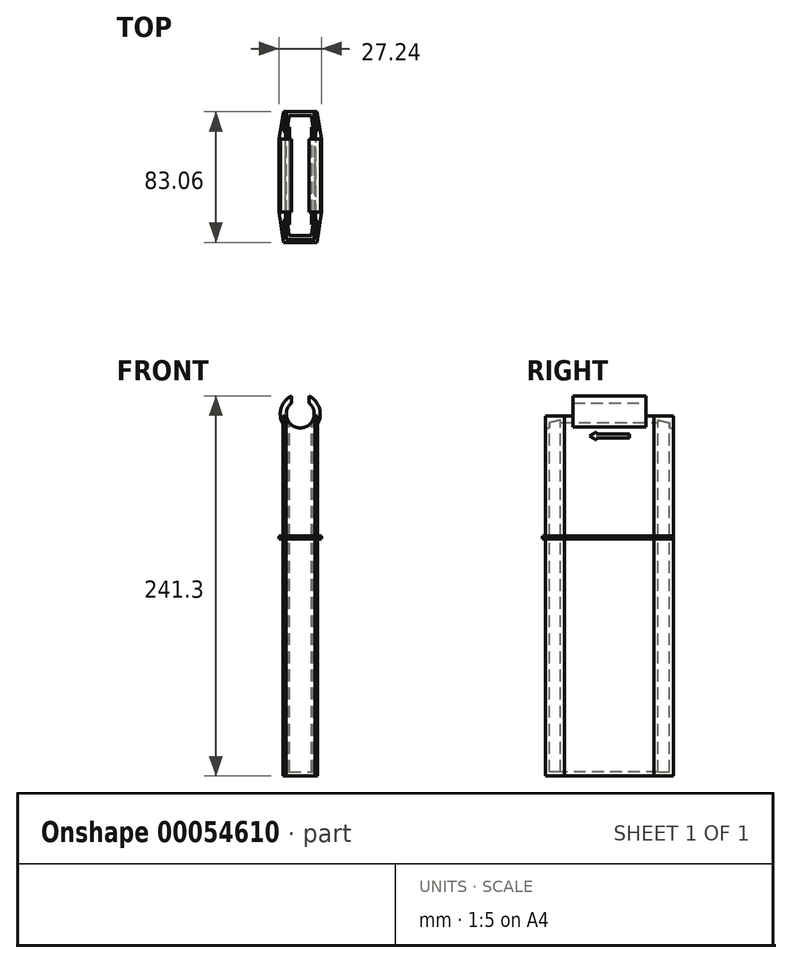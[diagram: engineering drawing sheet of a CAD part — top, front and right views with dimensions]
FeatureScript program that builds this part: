
annotation { "Feature Type Name" : "Feature", "Feature Type Description" : "" }
export const myFeature = defineFeature(function(context is Context, id is Id, definition is map)
    precondition{}
    {
        {
            var Q0;
            Q0=qCreatedBy(makeId("Top.planeOp"),FACE);
            cPlane(context, id + "F0", {"entities" : qUnion([Q0]), "cplaneType" : CPlaneType.OFFSET, "offset" : 76.2 * mm, "oppositeDirection" : true, "width" : 152.4 * mm, "height" : 152.4 * mm});
        }
        {
            var Q0;
            Q0=qCreatedBy(makeId("Top.planeOp"),FACE);
            var sketch = newSketch(context, id + "F1", { "sketchPlane" : qUnion([Q0])});
            skLineSegment(sketch, "E0", {"start": v(0, 97.88) * mm, "end": v(0, -104.86) * mm, "construction": true});
            skPoint(sketch, "E1.rect.middle", {"position": v(0, 0) * mm});
            skLineSegment(sketch, "E2", {"start": v(-10.99, 28.38) * mm, "end": v(-9.2, 40.64) * mm});
            skLineSegment(sketch, "E3", {"start": v(-9.2, 40.64) * mm, "end": v(9.2, 40.64) * mm});
            skLineSegment(sketch, "E4", {"start": v(9.2, 40.64) * mm, "end": v(10.99, 28.38) * mm});
            skLineSegment(sketch, "E5", {"start": v(-10.99, 28.38) * mm, "end": v(-9.52, 28.38) * mm});
            skLineSegment(sketch, "E6", {"start": v(-9.52, 28.38) * mm, "end": v(-9.52, -28.38) * mm});
            skLineSegment(sketch, "E7", {"start": v(-9.52, -28.38) * mm, "end": v(-10.99, -28.38) * mm});
            skLineSegment(sketch, "E8", {"start": v(-10.99, -28.38) * mm, "end": v(-9.2, -40.64) * mm});
            skLineSegment(sketch, "E9", {"start": v(-9.2, -40.64) * mm, "end": v(9.2, -40.64) * mm});
            skLineSegment(sketch, "E10", {"start": v(9.2, -40.64) * mm, "end": v(10.99, -28.38) * mm});
            skLineSegment(sketch, "E11", {"start": v(10.99, -28.38) * mm, "end": v(9.53, -28.38) * mm});
            skLineSegment(sketch, "E12", {"start": v(9.53, -28.38) * mm, "end": v(9.53, 28.38) * mm});
            skLineSegment(sketch, "E13", {"start": v(9.53, 28.38) * mm, "end": v(10.99, 28.38) * mm});
            skLineSegment(sketch, "E14", {"start": v(-33.77, 40.64) * mm, "end": v(28.62, 40.64) * mm, "construction": true});
            skLineSegment(sketch, "E15", {"start": v(-32.51, -40.64) * mm, "end": v(39.56, -40.64) * mm, "construction": true});
            skLineSegment(sketch, "E16", {"start": v(42.78, 0) * mm, "end": v(-43.09, 0) * mm, "construction": true});
            skSolve(sketch);
        }
        {
            var Q0;
            Q0=makeQuery(id+"F1.imprint","IMPRINT",FACE,{"disambiguationData":[TD([[makeQuery(id+"F1.imprint","IMPRINT",EDGE,{"derivedFrom":sQuery(id+"F1.wireOp",EDGE,"E2")}),-1.0]])]});
            extrude(context, id + "F2", {"entities" : qUnion([Q0]), "oppositeDirection" : true, "depth" : 228.6 * mm});
        }
        {
            var Q0;
            Q0=makeQuery(id+"F2.opExtrude","CAP_FACE",FACE,{"disambiguationData":[OSD([sQuery(id+"F1.wireOp",EDGE,"E2"),sQuery(id+"F1.wireOp",EDGE,"E3"),sQuery(id+"F1.wireOp",EDGE,"E4"),sQuery(id+"F1.wireOp",EDGE,"E5"),sQuery(id+"F1.wireOp",EDGE,"E6"),sQuery(id+"F1.wireOp",EDGE,"E7"),sQuery(id+"F1.wireOp",EDGE,"E8"),sQuery(id+"F1.wireOp",EDGE,"E9"),sQuery(id+"F1.wireOp",EDGE,"E10"),sQuery(id+"F1.wireOp",EDGE,"E11"),sQuery(id+"F1.wireOp",EDGE,"E12"),sQuery(id+"F1.wireOp",EDGE,"E13")])],"isStart":true});
            shell(context, id + "F3", {"entities" : qUnion([Q0]), "thickness" : 2.54 * mm});
        }
        {
            var Q0;
            Q0=qCreatedBy(makeId("Front.planeOp"),FACE);
            var sketch = newSketch(context, id + "F4", { "sketchPlane" : qUnion([Q0])});
            skLineSegment(sketch, "E17", {"start": v(0, 1.27) * mm, "end": v(0, 0) * mm, "construction": true});
            skArc(sketch, "E18", {"start": v(-5.54, 12.7) * mm, "mid": v(-12.67, 2.1) * mm, "end": v(-6.99, -9.34) * mm});
            skLineSegment(sketch, "E19", {"start": v(0, 1.27) * mm, "end": v(0, 13.97) * mm, "construction": true});
            skLineSegment(sketch, "E20", {"start": v(5.54, 12.7) * mm, "end": v(-5.54, 12.7) * mm, "construction": true});
            skArc(sketch, "E21", {"start": v(-5.54, 8.22) * mm, "mid": v(-8.83, 2.3) * mm, "end": v(-6.99, -4.23) * mm});
            skLineSegment(sketch, "E22", {"start": v(-5.54, 12.7) * mm, "end": v(-5.54, 8.22) * mm});
            skLineSegment(sketch, "E23", {"start": v(5.54, 12.7) * mm, "end": v(5.54, 8.22) * mm});
            skLineSegment(sketch, "E24", {"start": v(-6.98, -4.23) * mm, "end": v(-6.98, -9.34) * mm});
            skLineSegment(sketch, "E25", {"start": v(6.99, -4.23) * mm, "end": v(6.99, -9.34) * mm});
            skArc(sketch, "E26.trimOffspring", {"start": v(6.98, -4.23) * mm, "mid": v(8.83, 2.3) * mm, "end": v(5.54, 8.22) * mm});
            skArc(sketch, "E27.trimOffspring", {"start": v(6.98, -9.34) * mm, "mid": v(12.67, 2.1) * mm, "end": v(5.54, 12.7) * mm});
            skSolve(sketch);
        }
        {
            var Q0;
            Q0=makeQuery(id+"F4.imprint","IMPRINT",FACE,{"disambiguationData":[TD([[makeQuery(id+"F4.imprint","IMPRINT",EDGE,{"derivedFrom":sQuery(id+"F4.wireOp",EDGE,"E18")}),1.0]])]});
            var Q1;
            Q1=makeQuery(id+"F4.imprint","IMPRINT",FACE,{"disambiguationData":[TD([[makeQuery(id+"F4.imprint","IMPRINT",EDGE,{"derivedFrom":sQuery(id+"F4.wireOp",EDGE,"E23")}),1.0]])]});
            extrude(context, id + "F5", {"entities" : qUnion([Q0, Q1]), "operationType" : NewBodyOperationType.ADD, "endBound" : BoundingType.SYMMETRIC, "depth" : 46.23 * mm});
        }
        {
            var Q0;
            Q0=qCreatedBy(id+"F0.planeOp",FACE);
            var sketch = newSketch(context, id + "F6", { "sketchPlane" : qUnion([Q0])});
            skLineSegment(sketch, "E28", {"start": v(-13.62, -23.11) * mm, "end": v(-10.8, -42.42) * mm});
            skLineSegment(sketch, "E29", {"start": v(-10.8, -42.42) * mm, "end": v(10.8, -42.42) * mm});
            skLineSegment(sketch, "E30", {"start": v(10.8, -42.42) * mm, "end": v(13.62, -23.11) * mm});
            skLineSegment(sketch, "E31", {"start": v(13.62, -23.11) * mm, "end": v(13.62, 23.11) * mm});
            skLineSegment(sketch, "E32", {"start": v(13.62, 23.11) * mm, "end": v(10.52, 40.64) * mm});
            skLineSegment(sketch, "E33", {"start": v(10.52, 40.64) * mm, "end": v(-10.52, 40.64) * mm});
            skLineSegment(sketch, "E34", {"start": v(-10.52, 40.64) * mm, "end": v(-13.62, 23.11) * mm});
            skLineSegment(sketch, "E35", {"start": v(-13.62, 23.11) * mm, "end": v(-13.62, -23.11) * mm});
            skLineSegment(sketch, "E36", {"start": v(23.2, -23.11) * mm, "end": v(-20.93, -23.11) * mm, "construction": true});
            skLineSegment(sketch, "E37", {"start": v(19.25, 23.11) * mm, "end": v(-22.8, 23.11) * mm, "construction": true});
            skLineSegment(sketch, "E38", {"start": v(0, -56.67) * mm, "end": v(0, 46.95) * mm, "construction": true});
            skLineSegment(sketch, "E39", {"start": v(6.66, -70.61) * mm, "end": v(4.9, -70.36) * mm, "construction": true});
            skSolve(sketch);
        }
        {
            var Q0;
            Q0=makeQuery(id+"F6.imprint","IMPRINT",FACE,{"disambiguationData":[TD([[makeQuery(id+"F6.imprint","IMPRINT",EDGE,{"derivedFrom":sQuery(id+"F6.wireOp",EDGE,"E28")}),1.0]])]});
            extrude(context, id + "F7", {"entities" : qUnion([Q0]), "operationType" : NewBodyOperationType.ADD, "oppositeDirection" : true, "depth" : 1.78 * mm});
        }
        {
            var Q0;
            Q0=sQuery(id+"F4.wireOp",VERTEX,"E19.start");
            var Q1;
            Q1=makeQuery(id+"F2.opExtrude","SWEPT_BODY",BODY,{"disambiguationData":[OSD([sQuery(id+"F1.wireOp",EDGE,"E2"),sQuery(id+"F1.wireOp",EDGE,"E3"),sQuery(id+"F1.wireOp",EDGE,"E4"),sQuery(id+"F1.wireOp",EDGE,"E5"),sQuery(id+"F1.wireOp",EDGE,"E6"),sQuery(id+"F1.wireOp",EDGE,"E7"),sQuery(id+"F1.wireOp",EDGE,"E8"),sQuery(id+"F1.wireOp",EDGE,"E9"),sQuery(id+"F1.wireOp",EDGE,"E10"),sQuery(id+"F1.wireOp",EDGE,"E11"),sQuery(id+"F1.wireOp",EDGE,"E12"),sQuery(id+"F1.wireOp",EDGE,"E13")])]});
            hole(context, id + "F8", {"style" : HoleStyle.SIMPLE, "holeDiameter" : 17.78 * mm, "endStyle" : HoleEndStyle.THROUGH, "oppositeDirection" : true, "locations" : qUnion([Q0]), "scope" : qUnion([Q1])});
        }
        {
            var Q0;
            Q0=sQuery(id+"F4.wireOp",VERTEX,"E19.start");
            var Q1;
            Q1=makeQuery(id+"F2.opExtrude","SWEPT_BODY",BODY,{"disambiguationData":[OSD([sQuery(id+"F1.wireOp",EDGE,"E2"),sQuery(id+"F1.wireOp",EDGE,"E3"),sQuery(id+"F1.wireOp",EDGE,"E4"),sQuery(id+"F1.wireOp",EDGE,"E5"),sQuery(id+"F1.wireOp",EDGE,"E6"),sQuery(id+"F1.wireOp",EDGE,"E7"),sQuery(id+"F1.wireOp",EDGE,"E8"),sQuery(id+"F1.wireOp",EDGE,"E9"),sQuery(id+"F1.wireOp",EDGE,"E10"),sQuery(id+"F1.wireOp",EDGE,"E11"),sQuery(id+"F1.wireOp",EDGE,"E12"),sQuery(id+"F1.wireOp",EDGE,"E13")])]});
            hole(context, id + "F9", {"style" : HoleStyle.SIMPLE, "holeDiameter" : 17.78 * mm, "endStyle" : HoleEndStyle.THROUGH, "locations" : qUnion([Q0]), "scope" : qUnion([Q1])});
        }
        {
            var Q0;
            {var subQ0=sQuery(id+"F4.wireOp",EDGE,"E27.trimOffspring");var subQ6=sQuery(id+"F1.wireOp",EDGE,"E12");Q0=makeQuery(id+"F7.boolean.opBoolean","SPLIT",FACE,{"disambiguationData":[TD([makeQuery(id+"F5.opExtrude","SWEPT_FACE",FACE,{"disambiguationData":[OSD([subQ0])]})])],"derivedFrom":makeQuery(id+"F2.opExtrude","SWEPT_FACE",FACE,{"disambiguationData":[OSD([subQ6])]})});}
            var sketch = newSketch(context, id + "F10", { "sketchPlane" : qUnion([Q0])});
            skLineSegment(sketch, "E40", {"start": v(-8.3, -11.43) * mm, "end": v(12.7, -11.43) * mm});
            skLineSegment(sketch, "E41", {"start": v(12.7, -11.43) * mm, "end": v(12.7, -13.97) * mm});
            skLineSegment(sketch, "E42", {"start": v(12.7, -13.97) * mm, "end": v(-8.3, -13.97) * mm});
            skLineSegment(sketch, "E43", {"start": v(-8.3, -13.97) * mm, "end": v(-8.3, -15.24) * mm});
            skLineSegment(sketch, "E44", {"start": v(-8.3, -15.24) * mm, "end": v(-12.7, -12.7) * mm});
            skLineSegment(sketch, "E45", {"start": v(-12.7, -12.7) * mm, "end": v(-8.3, -10.16) * mm});
            skLineSegment(sketch, "E46", {"start": v(-8.3, -10.16) * mm, "end": v(-8.3, -11.43) * mm});
            skLineSegment(sketch, "E47", {"start": v(12.7, -12.7) * mm, "end": v(-12.7, -12.7) * mm, "construction": true});
            skLineSegment(sketch, "E48", {"start": v(-8.3, -11.43) * mm, "end": v(-8.3, -13.97) * mm, "construction": true});
            skPoint(sketch, "E49", {"position": v(0, -12.7) * mm});
            skLineSegment(sketch, "E50", {"start": v(0, 0) * mm, "end": v(0, -12.7) * mm, "construction": true});
            skSolve(sketch);
        }
        {
            var Q0;
            Q0=makeQuery(id+"F10.imprint","IMPRINT",FACE,{"disambiguationData":[TD([[makeQuery(id+"F10.imprint","IMPRINT",EDGE,{"derivedFrom":sQuery(id+"F10.wireOp",EDGE,"E40")}),-1.0]])]});
            extrude(context, id + "F11", {"entities" : qUnion([Q0]), "operationType" : NewBodyOperationType.REMOVE, "oppositeDirection" : true, "depth" : 0.25 * mm});
        }
    });
